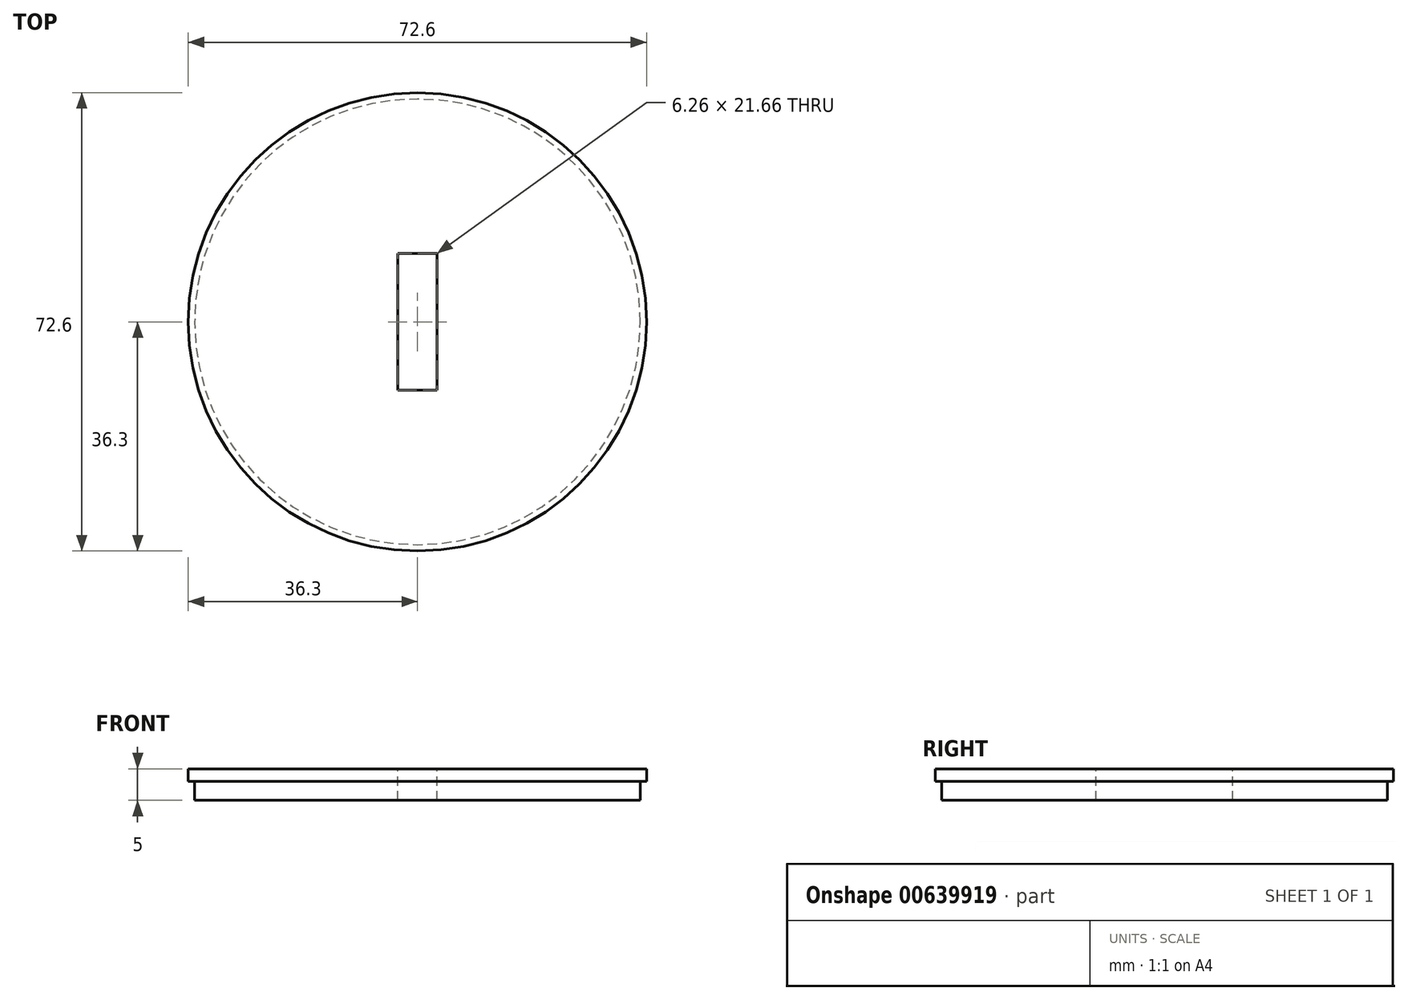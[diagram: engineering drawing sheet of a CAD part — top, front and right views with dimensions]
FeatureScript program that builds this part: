
annotation { "Feature Type Name" : "Feature", "Feature Type Description" : "" }
export const myFeature = defineFeature(function(context is Context, id is Id, definition is map)
    precondition{}
    {
        {
            var Q0;
            Q0=qCreatedBy(makeId("Top.planeOp"),FACE);
            var sketch = newSketch(context, id + "F0", { "sketchPlane" : qUnion([Q0])});
            skCircle(sketch, "E0", {"center": v(0, 0) * mm, "radius": 35.3 * mm});
            skSolve(sketch);
        }
        {
            var Q0;
            Q0=qSketchRegion(id+"F0",true);
            extrude(context, id + "F1", {"entities" : qUnion([Q0]), "depth" : 3 * mm, "offsetDistance" : 25 * mm});
        }
        {
            var Q0;
            Q0=makeQuery(id+"F1.opExtrude","CAP_FACE",FACE,{"disambiguationData":[OSD([sQuery(id+"F0.wireOp",EDGE,"E0")])],"isStart":false});
            cPlane(context, id + "F2", {"entities" : qUnion([Q0]), "cplaneType" : CPlaneType.OFFSET, "offset" : 0 * mm, "width" : 150 * mm, "height" : 150 * mm});
        }
        {
            var Q0;
            Q0=qCreatedBy(id+"F2.planeOp",FACE);
            var sketch = newSketch(context, id + "F3", { "sketchPlane" : qUnion([Q0])});
            skCircle(sketch, "E1", {"center": v(0, 0) * mm, "radius": 36.3 * mm});
            skSolve(sketch);
        }
        {
            var Q0;
            Q0=qSketchRegion(id+"F3",true);
            extrude(context, id + "F4", {"entities" : qUnion([Q0]), "operationType" : NewBodyOperationType.ADD, "depth" : 2 * mm, "offsetDistance" : 25 * mm});
        }
        {
            var Q0;
            Q0=makeQuery(id+"F4.opExtrude","CAP_FACE",FACE,{"disambiguationData":[OSD([sQuery(id+"F3.wireOp",EDGE,"E1")])],"isStart":false});
            var sketch = newSketch(context, id + "F5", { "sketchPlane" : qUnion([Q0])});
            skLineSegment(sketch, "E2.bottom", {"start": v(-3.13, 10.83) * mm, "end": v(3.13, 10.83) * mm});
            skLineSegment(sketch, "E2.top", {"start": v(-3.13, -10.83) * mm, "end": v(3.13, -10.83) * mm});
            skLineSegment(sketch, "E2.left", {"start": v(-3.13, 10.83) * mm, "end": v(-3.13, -10.83) * mm});
            skLineSegment(sketch, "E2.right", {"start": v(3.13, 10.83) * mm, "end": v(3.13, -10.83) * mm});
            skSolve(sketch);
        }
        {
            var Q0;
            Q0=makeQuery(id+"F5.imprint","IMPRINT",FACE,{"disambiguationData":[TD([[makeQuery(id+"F5.imprint","IMPRINT",EDGE,{"derivedFrom":sQuery(id+"F5.wireOp",EDGE,"E2.bottom")}),-1.0]])]});
            extrude(context, id + "F6", {"entities" : qUnion([Q0]), "operationType" : NewBodyOperationType.REMOVE, "oppositeDirection" : true, "depth" : 25 * mm, "offsetDistance" : 25 * mm});
        }
    });
